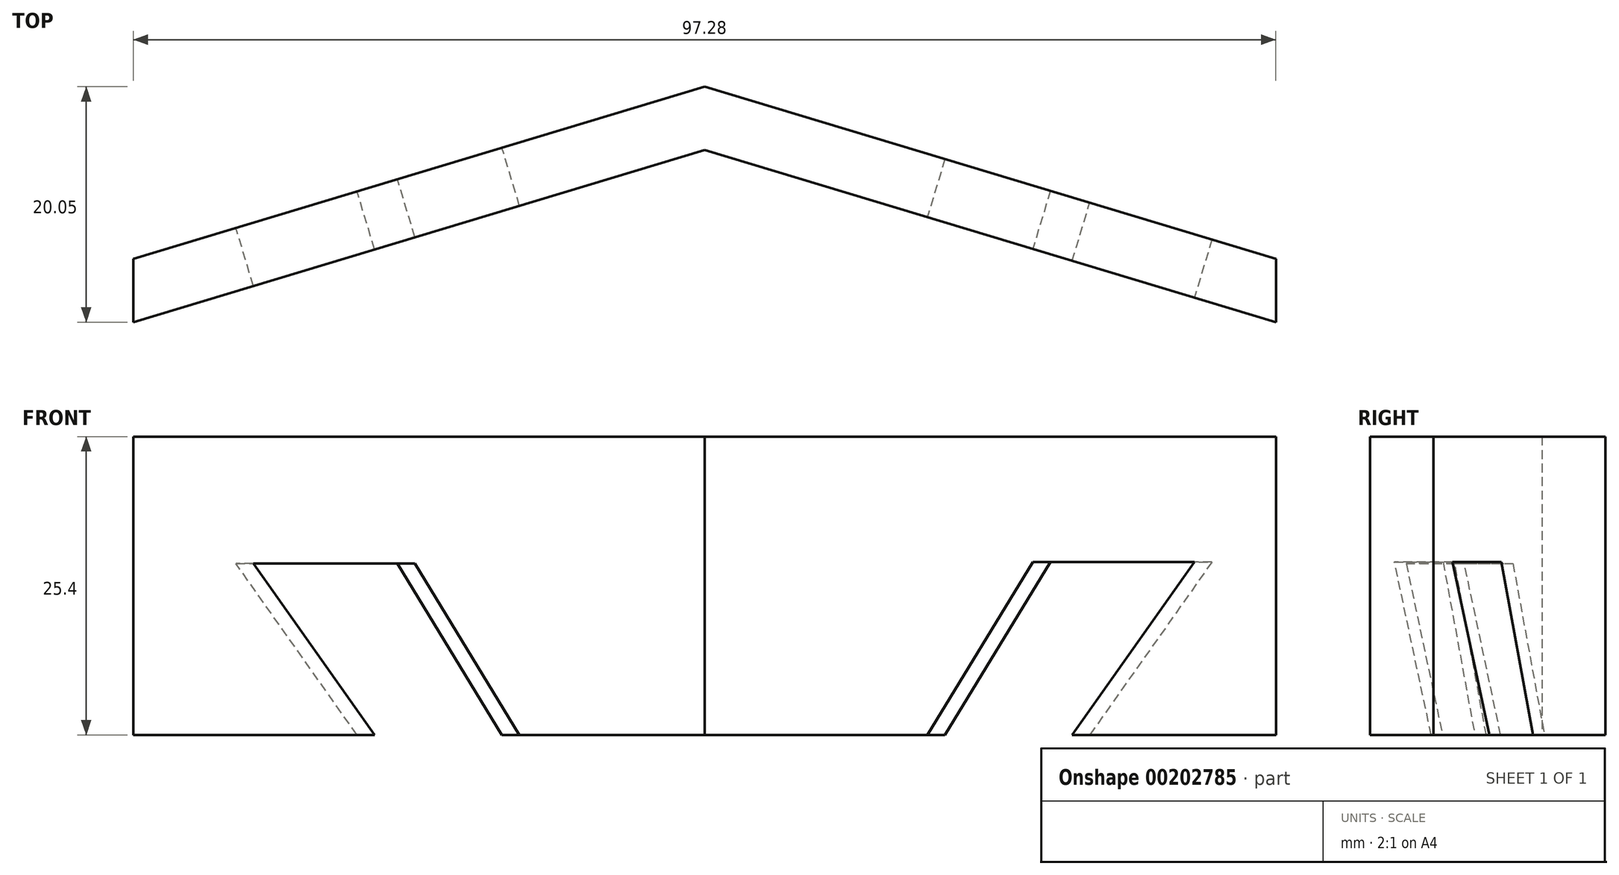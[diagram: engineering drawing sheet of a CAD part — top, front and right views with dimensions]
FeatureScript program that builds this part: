
annotation { "Feature Type Name" : "Feature", "Feature Type Description" : "" }
export const myFeature = defineFeature(function(context is Context, id is Id, definition is map)
    precondition{}
    {
        {
            var Q0;
            Q0=qCreatedBy(makeId("Top.planeOp"),FACE);
            var sketch = newSketch(context, id + "F0", { "sketchPlane" : qUnion([Q0])});
            skLineSegment(sketch, "E0", {"start": v(0, 37.45) * mm, "end": v(-48.64, 22.8) * mm});
            skLineSegment(sketch, "E1", {"start": v(0, 25.27) * mm, "end": v(0, 60.42) * mm, "construction": true});
            skLineSegment(sketch, "E2", {"start": v(0, 37.45) * mm, "end": v(0, 42.84) * mm});
            skLineSegment(sketch, "E3", {"start": v(0, 42.84) * mm, "end": v(-48.64, 28.2) * mm});
            skLineSegment(sketch, "E4", {"start": v(-48.64, 28.2) * mm, "end": v(-48.64, 22.8) * mm});
            skLineSegment(sketch, "E5.MirrorCS", {"start": v(0, 37.45) * mm, "end": v(48.64, 22.8) * mm});
            skLineSegment(sketch, "E6.MirrorCS", {"start": v(48.64, 28.2) * mm, "end": v(48.64, 22.8) * mm});
            skLineSegment(sketch, "E7.MirrorCS", {"start": v(0, 42.84) * mm, "end": v(48.64, 28.2) * mm});
            skSolve(sketch);
        }
        {
            var Q0;
            Q0 = qSketchRegion(id + "F0", true);
            extrude(context, id + "F1", {"entities" : qUnion([Q0]), "depth" : 25.4 * mm});
        }
        {
            var Q0;
            Q0=makeQuery(id+"F1.opExtrude","SWEPT_FACE",FACE,{"disambiguationData":[OSD([sQuery(id+"F0.wireOp",EDGE,"E3")])]});
            var sketch = newSketch(context, id + "F2", { "sketchPlane" : qUnion([Q0])});
            skLineSegment(sketch, "E8", {"start": v(18.53, 0) * mm, "end": v(29.3, 14.6) * mm});
            skLineSegment(sketch, "E9", {"start": v(29.3, 14.6) * mm, "end": v(14.94, 14.6) * mm});
            skLineSegment(sketch, "E10", {"start": v(14.94, 14.6) * mm, "end": v(5.65, 0) * mm});
            skLineSegment(sketch, "E11", {"start": v(5.65, 0) * mm, "end": v(18.53, 0) * mm});
            skSolve(sketch);
        }
        {
            var Q0;
            Q0 = qSketchRegion(id + "F2", true);
            var Q1;
            Q1=makeQuery(id+"F5cOMrSaVJb5Z2m_0.opExtrude","SWEPT_FACE",FACE,{"disambiguationData":[OSD([sQuery(id+"F0.wireOp",EDGE,"E0")])]});
            extrude(context, id + "F3", {"entities" : qUnion([Q0]), "operationType" : NewBodyOperationType.REMOVE, "endBound" : BoundingType.THROUGH_ALL, "oppositeDirection" : true, "endBoundEntityFace" : qUnion([Q1]), "depth" : 25.4 * mm});
        }
        {
            var Q0;
            Q0=makeQuery(id+"F1.opExtrude","SWEPT_FACE",FACE,{"disambiguationData":[OSD([sQuery(id+"F0.wireOp",EDGE,"E5.MirrorCS")])]});
            var sketch = newSketch(context, id + "F4", { "sketchPlane" : qUnion([Q0])});
            skLineSegment(sketch, "E12", {"start": v(21.98, 0.12) * mm, "end": v(32.76, 14.72) * mm});
            skLineSegment(sketch, "E13", {"start": v(32.76, 14.72) * mm, "end": v(18.4, 14.72) * mm});
            skLineSegment(sketch, "E14", {"start": v(18.4, 14.72) * mm, "end": v(9.1, 0.12) * mm});
            skLineSegment(sketch, "E15", {"start": v(9.1, 0.12) * mm, "end": v(21.98, 0.12) * mm});
            skSolve(sketch);
        }
        {
            var Q0;
            Q0 = qSketchRegion(id + "F4", true);
            extrude(context, id + "F5", {"entities" : qUnion([Q0]), "operationType" : NewBodyOperationType.REMOVE, "endBound" : BoundingType.THROUGH_ALL, "oppositeDirection" : true, "depth" : 25.4 * mm});
        }
        {
            var Q0;
            Q0=makeQuery(id+"F1.opExtrude","SWEPT_FACE",FACE,{"disambiguationData":[OSD([sQuery(id+"F0.wireOp",EDGE,"E7.MirrorCS")])]});
            var sketch = newSketch(context, id + "F6", { "sketchPlane" : qUnion([Q0])});
            skLineSegment(sketch, "E16", {"start": v(-25.24, 4.54) * mm, "end": v(-17.44, -6.04) * mm});
            skLineSegment(sketch, "E17", {"start": v(-12.57, 5.58) * mm, "end": v(-5.6, -5.39) * mm});
            skLineSegment(sketch, "E18", {"start": v(-5.6, -5.39) * mm, "end": v(-17.44, -6.04) * mm});
            skLineSegment(sketch, "E19", {"start": v(-25.24, 4.54) * mm, "end": v(-12.57, 5.58) * mm});
            skSolve(sketch);
        }
        {
            var Q0;
            Q0 = qSketchRegion(id + "F6", true);
            extrude(context, id + "F7", {"entities" : qUnion([Q0]), "operationType" : NewBodyOperationType.REMOVE, "endBound" : BoundingType.THROUGH_ALL, "oppositeDirection" : true, "depth" : 25.4 * mm});
        }
    });
